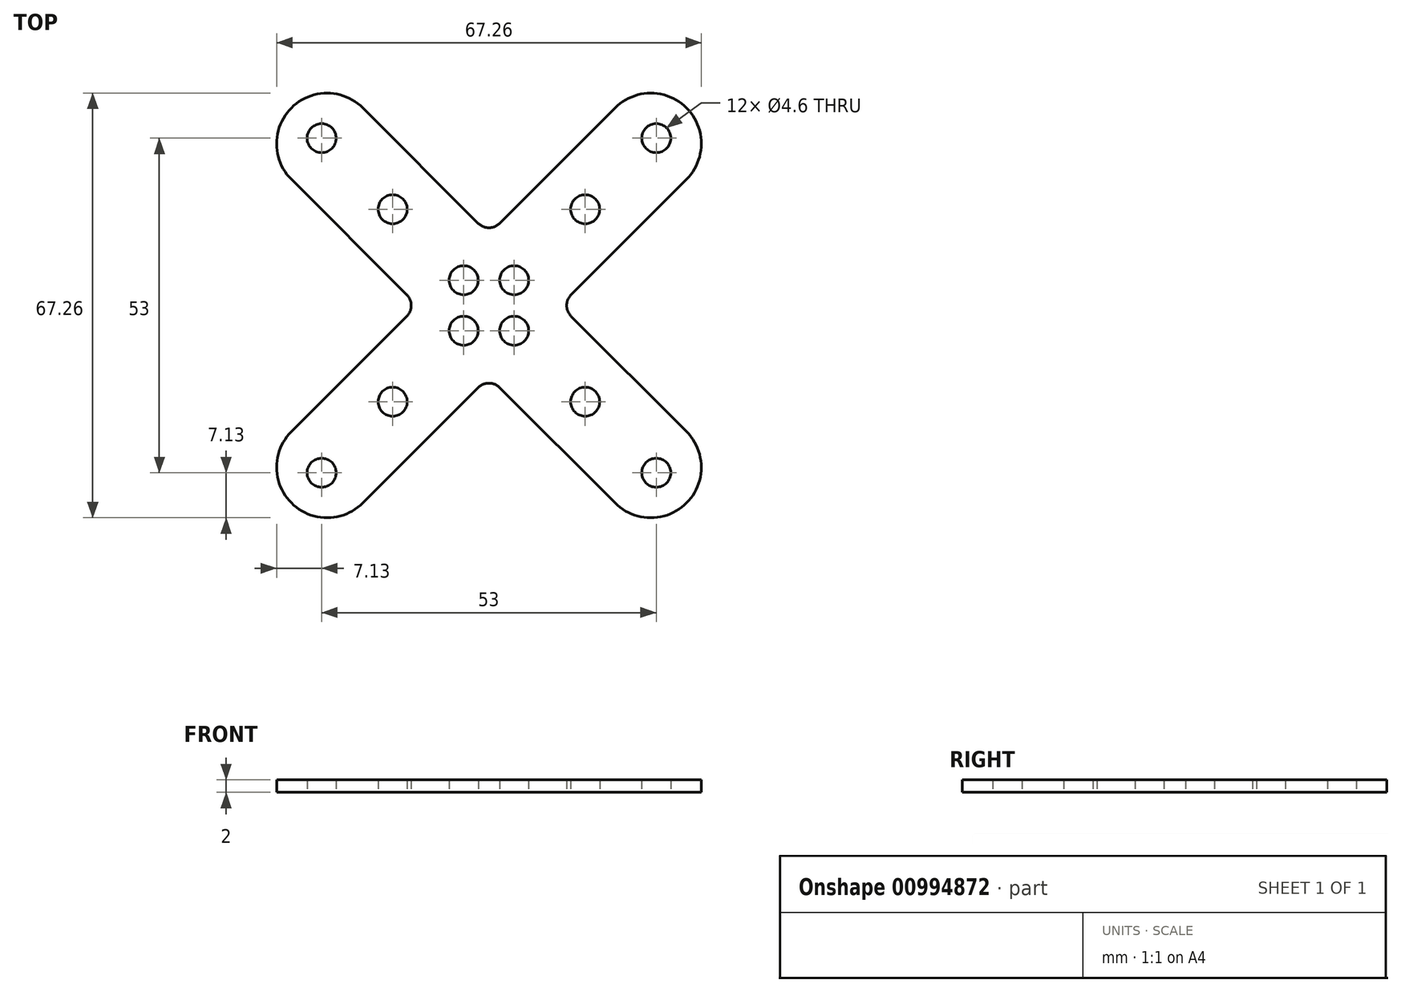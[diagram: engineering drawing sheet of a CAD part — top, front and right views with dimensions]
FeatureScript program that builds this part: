
annotation { "Feature Type Name" : "Feature", "Feature Type Description" : "" }
export const myFeature = defineFeature(function(context is Context, id is Id, definition is map)
    precondition{}
    {
        {
            var Q0;
            Q0=qCreatedBy(makeId("Top.planeOp"),FACE);
            var sketch = newSketch(context, id + "F0", { "sketchPlane" : qUnion([Q0])});
            skCircle(sketch, "E0", {"center": v(4, 4) * mm, "radius": 2.3 * mm});
            skCircle(sketch, "E1", {"center": v(15.25, 15.25) * mm, "radius": 2.3 * mm});
            skCircle(sketch, "E2", {"center": v(26.5, 26.5) * mm, "radius": 2.3 * mm});
            skLineSegment(sketch, "E3", {"start": v(36.95, 25.63) * mm, "end": v(11.31, 0) * mm});
            skLineSegment(sketch, "E4", {"start": v(11.31, 0) * mm, "end": v(0, 0) * mm});
            skLineSegment(sketch, "E5", {"start": v(25.63, 36.95) * mm, "end": v(0, 11.31) * mm});
            skLineSegment(sketch, "E6", {"start": v(0, 11.31) * mm, "end": v(0, 0) * mm});
            skLineSegment(sketch, "E7", {"start": v(0, 0) * mm, "end": v(42.07, 42.07) * mm, "construction": true});
            skLineSegment(sketch, "E8", {"start": v(31.29, 31.29) * mm, "end": v(36.95, 25.63) * mm});
            skLineSegment(sketch, "E9", {"start": v(31.29, 31.29) * mm, "end": v(25.63, 36.95) * mm});
            skLineSegment(sketch, "E10.trimOffspring", {"start": v(43.19, 43.19) * mm, "end": v(52.48, 52.48) * mm, "construction": true});
            skCircle(sketch, "E11", {"center": v(4, 4) * mm, "radius": 4 * mm, "construction": true});
            skLineSegment(sketch, "E12", {"start": v(12.31, 0) * mm, "end": v(12.31, 1) * mm});
            skLineSegment(sketch, "E13.MirrorCS", {"start": v(0, 12.31) * mm, "end": v(1, 12.31) * mm});
            skLineSegment(sketch, "E14", {"start": v(12.31, 0) * mm, "end": v(11.31, 0) * mm});
            skLineSegment(sketch, "E15", {"start": v(0, 12.31) * mm, "end": v(0, 11.31) * mm});
            skSolve(sketch);
        }
        {
            var Q0;
            Q0=makeQuery(id+"F0.imprint","IMPRINT",FACE,{"disambiguationData":[TD([[makeQuery(id+"F0.imprint","IMPRINT",EDGE,{"derivedFrom":sQuery(id+"F0.wireOp",EDGE,"E0")}),-1.0]])]});
            var Q1;
            {var subQ2=sQuery(id+"F0.wireOp",EDGE,"E13.MirrorCS");Q1=makeQuery(id+"F0.imprint","IMPRINT",FACE,{"disambiguationData":[TD([[makeQuery(id+"F0.imprint","IMPRINT",EDGE,{"derivedFrom":subQ2}),-1.0]])]});}
            var Q2;
            {var subQ2=sQuery(id+"F0.wireOp",EDGE,"E12");Q2=makeQuery(id+"F0.imprint","IMPRINT",FACE,{"disambiguationData":[TD([[makeQuery(id+"F0.imprint","IMPRINT",EDGE,{"derivedFrom":subQ2}),1.0]])]});}
            extrude(context, id + "F1", {"entities" : qUnion([Q0, Q1, Q2]), "depth" : 2 * mm, "offsetDistance" : 25 * mm});
        }
        {
            var Q0;
            Q0=makeQuery(id+"F1.opExtrude","SWEPT_BODY",BODY,{"disambiguationData":[OSD([sQuery(id+"F0.wireOp",EDGE,"E0"),sQuery(id+"F0.wireOp",EDGE,"E1"),sQuery(id+"F0.wireOp",EDGE,"E2"),sQuery(id+"F0.wireOp",EDGE,"E3"),sQuery(id+"F0.wireOp",EDGE,"E4"),sQuery(id+"F0.wireOp",EDGE,"E5"),sQuery(id+"F0.wireOp",EDGE,"E6"),sQuery(id+"F0.wireOp",EDGE,"EbnRSb0D-1guQ-8x5C-nXOE-OeIXNMyvbWJn")])]});
            var Q1;
            Q1=qCreatedBy(makeId("Right.planeOp"),FACE);
            mirror(context, id + "F2", {"operationType" : NewBodyOperationType.ADD, "entities" : qUnion([Q0]), "mirrorPlane" : qUnion([Q1])});
        }
        {
            var Q0;
            Q0=makeQuery(id+"F1.opExtrude","SWEPT_BODY",BODY,{"disambiguationData":[OSD([sQuery(id+"F0.wireOp",EDGE,"E0"),sQuery(id+"F0.wireOp",EDGE,"E1"),sQuery(id+"F0.wireOp",EDGE,"E2"),sQuery(id+"F0.wireOp",EDGE,"E3"),sQuery(id+"F0.wireOp",EDGE,"E4"),sQuery(id+"F0.wireOp",EDGE,"E5"),sQuery(id+"F0.wireOp",EDGE,"E6"),sQuery(id+"F0.wireOp",EDGE,"EbnRSb0D-1guQ-8x5C-nXOE-OeIXNMyvbWJn")])]});
            var Q1;
            Q1=qCreatedBy(makeId("Front.planeOp"),FACE);
            mirror(context, id + "F3", {"operationType" : NewBodyOperationType.ADD, "entities" : qUnion([Q0]), "mirrorPlane" : qUnion([Q1])});
        }
        {
            var Q0;
            Q0=makeQuery(id+"F2.opPattern","COPY",EDGE,{"derivedFrom":makeQuery(id+"F1.opExtrude","SWEPT_EDGE",EDGE,{"disambiguationData":[OSD([sQuery(id+"F0.wireOp",EDGE,"E5"),sQuery(id+"F0.wireOp",EDGE,"E9")])]}),"instanceName":"1"});
            var Q1;
            Q1=makeQuery(id+"F2.opPattern","COPY",EDGE,{"derivedFrom":makeQuery(id+"F1.opExtrude","SWEPT_EDGE",EDGE,{"disambiguationData":[OSD([sQuery(id+"F0.wireOp",EDGE,"E3"),sQuery(id+"F0.wireOp",EDGE,"E8")])]}),"instanceName":"1"});
            var Q2;
            Q2=makeQuery(id+"F3.opPattern","COPY",EDGE,{"derivedFrom":makeQuery(id+"F2.opPattern","COPY",EDGE,{"derivedFrom":makeQuery(id+"F1.opExtrude","SWEPT_EDGE",EDGE,{"disambiguationData":[OSD([sQuery(id+"F0.wireOp",EDGE,"E3"),sQuery(id+"F0.wireOp",EDGE,"E8")])]}),"instanceName":"1"}),"instanceName":"1"});
            var Q3;
            Q3=makeQuery(id+"F3.opPattern","COPY",EDGE,{"derivedFrom":makeQuery(id+"F2.opPattern","COPY",EDGE,{"derivedFrom":makeQuery(id+"F1.opExtrude","SWEPT_EDGE",EDGE,{"disambiguationData":[OSD([sQuery(id+"F0.wireOp",EDGE,"E5"),sQuery(id+"F0.wireOp",EDGE,"E9")])]}),"instanceName":"1"}),"instanceName":"1"});
            var Q4;
            Q4=makeQuery(id+"F3.opPattern","COPY",EDGE,{"derivedFrom":makeQuery(id+"F1.opExtrude","SWEPT_EDGE",EDGE,{"disambiguationData":[OSD([sQuery(id+"F0.wireOp",EDGE,"E5"),sQuery(id+"F0.wireOp",EDGE,"E9")])]}),"instanceName":"1"});
            var Q5;
            Q5=makeQuery(id+"F3.opPattern","COPY",EDGE,{"derivedFrom":makeQuery(id+"F1.opExtrude","SWEPT_EDGE",EDGE,{"disambiguationData":[OSD([sQuery(id+"F0.wireOp",EDGE,"E3"),sQuery(id+"F0.wireOp",EDGE,"E8")])]}),"instanceName":"1"});
            var Q6;
            Q6=makeQuery(id+"F1.opExtrude","SWEPT_EDGE",EDGE,{"disambiguationData":[OSD([sQuery(id+"F0.wireOp",EDGE,"E3"),sQuery(id+"F0.wireOp",EDGE,"E8")])]});
            var Q7;
            Q7=makeQuery(id+"F1.opExtrude","SWEPT_EDGE",EDGE,{"disambiguationData":[OSD([sQuery(id+"F0.wireOp",EDGE,"E5"),sQuery(id+"F0.wireOp",EDGE,"E9")])]});
            fillet(context, id + "F4", {"entities" : qUnion([Q0, Q1, Q2, Q3, Q4, Q5, Q6, Q7]), "radius" : 8 * mm, "tangentPropagation" : true, "defaultsChanged" : false, "vertexSettings" : [], "allowEdgeOverflow" : false});
        }
        {
            var Q0;
            Q0=makeQuery(id+"F1.opExtrude","SWEPT_EDGE",EDGE,{"disambiguationData":[OSD([sQuery(id+"F0.wireOp",EDGE,"E3"),sQuery(id+"F0.wireOp",EDGE,"E12")])]});
            var Q1;
            Q1=makeQuery(id+"F3.opPattern","COPY",EDGE,{"derivedFrom":makeQuery(id+"F1.opExtrude","SWEPT_EDGE",EDGE,{"disambiguationData":[OSD([sQuery(id+"F0.wireOp",EDGE,"E3"),sQuery(id+"F0.wireOp",EDGE,"E12")])]}),"instanceName":"1"});
            var Q2;
            Q2=makeQuery(id+"F1.opExtrude","SWEPT_EDGE",EDGE,{"disambiguationData":[OSD([sQuery(id+"F0.wireOp",EDGE,"E5"),sQuery(id+"F0.wireOp",EDGE,"E13.MirrorCS")])]});
            var Q3;
            Q3=makeQuery(id+"F2.opPattern","COPY",EDGE,{"derivedFrom":makeQuery(id+"F1.opExtrude","SWEPT_EDGE",EDGE,{"disambiguationData":[OSD([sQuery(id+"F0.wireOp",EDGE,"E5"),sQuery(id+"F0.wireOp",EDGE,"E13.MirrorCS")])]}),"instanceName":"1"});
            var Q4;
            Q4=makeQuery(id+"F2.opPattern","COPY",EDGE,{"derivedFrom":makeQuery(id+"F1.opExtrude","SWEPT_EDGE",EDGE,{"disambiguationData":[OSD([sQuery(id+"F0.wireOp",EDGE,"E3"),sQuery(id+"F0.wireOp",EDGE,"E12")])]}),"instanceName":"1"});
            var Q5;
            Q5=makeQuery(id+"F3.opPattern","COPY",EDGE,{"derivedFrom":makeQuery(id+"F2.opPattern","COPY",EDGE,{"derivedFrom":makeQuery(id+"F1.opExtrude","SWEPT_EDGE",EDGE,{"disambiguationData":[OSD([sQuery(id+"F0.wireOp",EDGE,"E3"),sQuery(id+"F0.wireOp",EDGE,"E12")])]}),"instanceName":"1"}),"instanceName":"1"});
            var Q6;
            Q6=makeQuery(id+"F3.opPattern","COPY",EDGE,{"derivedFrom":makeQuery(id+"F2.opPattern","COPY",EDGE,{"derivedFrom":makeQuery(id+"F1.opExtrude","SWEPT_EDGE",EDGE,{"disambiguationData":[OSD([sQuery(id+"F0.wireOp",EDGE,"E5"),sQuery(id+"F0.wireOp",EDGE,"E13.MirrorCS")])]}),"instanceName":"1"}),"instanceName":"1"});
            var Q7;
            Q7=makeQuery(id+"F3.opPattern","COPY",EDGE,{"derivedFrom":makeQuery(id+"F1.opExtrude","SWEPT_EDGE",EDGE,{"disambiguationData":[OSD([sQuery(id+"F0.wireOp",EDGE,"E5"),sQuery(id+"F0.wireOp",EDGE,"E13.MirrorCS")])]}),"instanceName":"1"});
            fillet(context, id + "F5", {"entities" : qUnion([Q0, Q1, Q2, Q3, Q4, Q5, Q6, Q7]), "tangentPropagation" : true, "radius" : 2.4 * mm, "defaultsChanged" : false, "vertexSettings" : [], "allowEdgeOverflow" : false});
        }
    });
